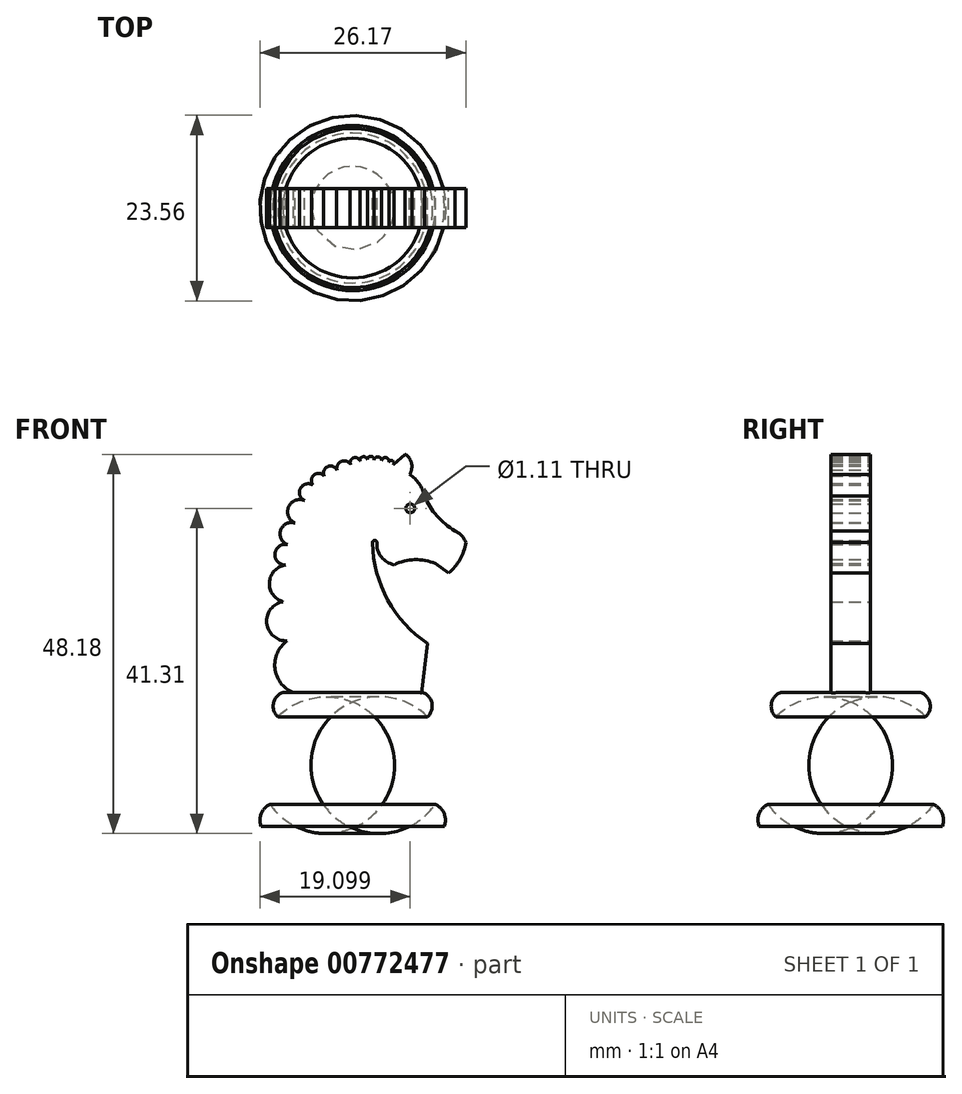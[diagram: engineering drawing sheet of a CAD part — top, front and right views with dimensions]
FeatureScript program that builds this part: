
annotation { "Feature Type Name" : "Feature", "Feature Type Description" : "" }
export const myFeature = defineFeature(function(context is Context, id is Id, definition is map)
    precondition{}
    {
        {
            var Q0;
            Q0=qCreatedBy(makeId("Front.planeOp"),FACE);
            var sketch = newSketch(context, id + "F0", { "sketchPlane" : qUnion([Q0])});
            skArc(sketch, "E0", {"start": v(-7.5, 42.75) * mm, "mid": v(-9.76, 30.83) * mm, "end": v(-7.05, 19.01) * mm});
            skArc(sketch, "E1", {"start": v(-1.21, 48.3) * mm, "mid": v(-4.94, 46.2) * mm, "end": v(-7.5, 42.75) * mm});
            skArc(sketch, "E2", {"start": v(4.28, 48.3) * mm, "mid": v(1.53, 48.79) * mm, "end": v(-1.21, 48.3) * mm});
            skLineSegment(sketch, "E3", {"start": v(7.79, 18.88) * mm, "end": v(8.6, 25.55) * mm});
            skArc(sketch, "E4", {"start": v(1.6, 38.32) * mm, "mid": v(3.5, 31.06) * mm, "end": v(8.6, 25.55) * mm});
            skArc(sketch, "E5", {"start": v(2.13, 38.38) * mm, "mid": v(1.83, 38.62) * mm, "end": v(1.6, 38.32) * mm});
            skArc(sketch, "E6", {"start": v(2.13, 38.38) * mm, "mid": v(2.7, 36.53) * mm, "end": v(4.36, 35.53) * mm});
            skArc(sketch, "E7", {"start": v(6.3, 47) * mm, "mid": v(6.55, 48.4) * mm, "end": v(5.74, 49.56) * mm});
            skLineSegment(sketch, "E8", {"start": v(4.28, 48.3) * mm, "end": v(5.74, 49.56) * mm});
            skArc(sketch, "E9", {"start": v(8.2, 44.27) * mm, "mid": v(7.5, 45.82) * mm, "end": v(6.3, 47) * mm});
            skArc(sketch, "E10", {"start": v(8.2, 44.27) * mm, "mid": v(9.77, 41.74) * mm, "end": v(12.07, 39.84) * mm});
            skArc(sketch, "E11", {"start": v(13.45, 38.34) * mm, "mid": v(12.9, 39.23) * mm, "end": v(12.07, 39.84) * mm});
            skArc(sketch, "E12", {"start": v(11.27, 34.47) * mm, "mid": v(12.7, 36.22) * mm, "end": v(13.45, 38.34) * mm});
            skArc(sketch, "E13", {"start": v(9.58, 35.67) * mm, "mid": v(6.95, 36.18) * mm, "end": v(4.36, 35.53) * mm});
            skLineSegment(sketch, "E14", {"start": v(9.58, 35.67) * mm, "end": v(11.27, 34.47) * mm});
            skLineSegment(sketch, "E15", {"start": v(-7.05, 19.01) * mm, "end": v(7.8, 19.01) * mm});
            skPoint(sketch, "E16.end.orphan", {"position": v(7.79, 16.62) * mm});
            skPoint(sketch, "E17.start.orphan", {"position": v(-7.5, 16.63) * mm});
            skLineSegment(sketch, "E18", {"start": v(8.67, 37.4) * mm, "end": v(11.27, 35.67) * mm});
            skCircle(sketch, "E19", {"center": v(6.38, 42.7) * mm, "radius": 0.56 * mm});
            skPoint(sketch, "E20.start.orphan", {"position": v(-11.68, 44.88) * mm});
            skPoint(sketch, "E21.end.orphan", {"position": v(-11.68, 43.37) * mm});
            skPoint(sketch, "E22.end.orphan", {"position": v(-11.68, 41.65) * mm});
            skPoint(sketch, "E23.start.orphan", {"position": v(-11.68, 39.8) * mm});
            skPoint(sketch, "E24.end.orphan", {"position": v(-8.9, 38.46) * mm});
            skPoint(sketch, "E24.start.orphan", {"position": v(-11.68, 38.46) * mm});
            skPoint(sketch, "E25.end.orphan", {"position": v(-11.68, 37.05) * mm});
            skPoint(sketch, "E26.orphan", {"position": v(-11.68, 35.66) * mm});
            skPoint(sketch, "E27.end.orphan", {"position": v(-9.5, 34.37) * mm});
            skPoint(sketch, "E28.end.orphan", {"position": v(-11.68, 34.37) * mm});
            skPoint(sketch, "E29.end.orphan", {"position": v(-11.68, 32.72) * mm});
            skPoint(sketch, "E30.end.orphan", {"position": v(-11.68, 30.9) * mm});
            skPoint(sketch, "E31.end.orphan", {"position": v(-11.68, 28.54) * mm});
            skPoint(sketch, "E32.end.orphan", {"position": v(-9.5, 27.44) * mm});
            skPoint(sketch, "E33.end.orphan", {"position": v(-11.68, 26.74) * mm});
            skArc(sketch, "E34", {"start": v(-7.01, 43.67) * mm, "mid": v(-9.08, 42.86) * mm, "end": v(-8.22, 40.82) * mm});
            skArc(sketch, "E35", {"start": v(-8.22, 40.82) * mm, "mid": v(-10.11, 39.85) * mm, "end": v(-9, 38.04) * mm});
            skArc(sketch, "E36", {"start": v(-9, 38.04) * mm, "mid": v(-10.78, 37.05) * mm, "end": v(-9.48, 35.49) * mm});
            skArc(sketch, "E37", {"start": v(-9.48, 35.49) * mm, "mid": v(-11.52, 33.27) * mm, "end": v(-9.76, 30.83) * mm});
            skArc(sketch, "E38", {"start": v(-9.76, 30.83) * mm, "mid": v(-11.86, 28.1) * mm, "end": v(-9.25, 25.87) * mm});
            skPoint(sketch, "E39.start.orphan", {"position": v(-8.9, 46.81) * mm});
            skPoint(sketch, "E40.end.orphan", {"position": v(-7.05, 48.12) * mm});
            skPoint(sketch, "E41.start.orphan", {"position": v(-4.94, 46.2) * mm});
            skPoint(sketch, "E42.end.orphan", {"position": v(0, 48.64) * mm});
            skPoint(sketch, "E43.start.orphan", {"position": v(1.53, 48.79) * mm});
            skArc(sketch, "E44", {"start": v(-5.72, 45.42) * mm, "mid": v(-7.48, 45.37) * mm, "end": v(-7.01, 43.67) * mm});
            skArc(sketch, "E45", {"start": v(-4.43, 46.61) * mm, "mid": v(-5.88, 46.9) * mm, "end": v(-5.72, 45.42) * mm});
            skArc(sketch, "E46", {"start": v(-2.94, 47.58) * mm, "mid": v(-4.23, 47.94) * mm, "end": v(-4.43, 46.61) * mm});
            skArc(sketch, "E47", {"start": v(-1.21, 48.3) * mm, "mid": v(-2.37, 48.65) * mm, "end": v(-2.94, 47.58) * mm});
            skArc(sketch, "E48", {"start": v(0, 48.64) * mm, "mid": v(-0.8, 49.13) * mm, "end": v(-1.21, 48.3) * mm});
            skArc(sketch, "E49", {"start": v(0.93, 48.77) * mm, "mid": v(0.4, 49.26) * mm, "end": v(0, 48.64) * mm});
            skArc(sketch, "E50", {"start": v(1.79, 48.79) * mm, "mid": v(1.35, 49.3) * mm, "end": v(0.93, 48.77) * mm});
            skArc(sketch, "E51", {"start": v(2.75, 48.7) * mm, "mid": v(2.32, 49.24) * mm, "end": v(1.79, 48.79) * mm});
            skArc(sketch, "E52", {"start": v(3.65, 48.5) * mm, "mid": v(3.32, 49.14) * mm, "end": v(2.75, 48.7) * mm});
            skArc(sketch, "E53", {"start": v(4.28, 48.3) * mm, "mid": v(4.08, 48.76) * mm, "end": v(3.65, 48.5) * mm});
            skArc(sketch, "E54", {"start": v(-9.25, 25.87) * mm, "mid": v(-9.52, 25.9) * mm, "end": v(-9.8, 25.9) * mm});
            skArc(sketch, "E55", {"start": v(-9.25, 25.87) * mm, "mid": v(-10.65, 21.64) * mm, "end": v(-7.05, 19.01) * mm});
            skSolve(sketch);
        }
        {
            var Q0;
            Q0=qSketchRegion(id+"F0",true);
            extrude(context, id + "F1", {"entities" : qUnion([Q0]), "endBound" : BoundingType.SYMMETRIC, "depth" : 5 * mm, "offsetDistance" : 25 * mm});
        }
        {
            var Q0;
            Q0=qCreatedBy(makeId("Front.planeOp"),FACE);
            var sketch = newSketch(context, id + "F2", { "sketchPlane" : qUnion([Q0])});
            skArc(sketch, "E56", {"start": v(-9.8, 19.32) * mm, "mid": v(-11, 17.95) * mm, "end": v(-10.44, 16.22) * mm});
            skArc(sketch, "E57", {"start": v(-10.44, 16.22) * mm, "mid": v(-12.96, 10.83) * mm, "end": v(-11.42, 5.08) * mm});
            skArc(sketch, "E58", {"start": v(-11.42, 5.08) * mm, "mid": v(-12.55, 3.92) * mm, "end": v(-12.57, 2.3) * mm});
            skLineSegment(sketch, "E59", {"start": v(-12.57, 2.3) * mm, "end": v(-0.93, 2.3) * mm});
            skLineSegment(sketch, "E60", {"start": v(-0.93, 2.3) * mm, "end": v(-0.93, 3.78) * mm});
            skLineSegment(sketch, "E61", {"start": v(-0.93, 19.3) * mm, "end": v(-0.93, 2.3) * mm});
            skLineSegment(sketch, "E62", {"start": v(-0.93, 19.3) * mm, "end": v(-9.8, 19.32) * mm});
            skSolve(sketch);
        }
        {
            var Q0;
            Q0=qSketchRegion(id+"F2",true);
            var Q1;
            Q1=sQuery(id+"F2.wireOp",EDGE,"E61");
            revolve(context, id + "F3", {"operationType" : NewBodyOperationType.ADD, "surfaceOperationType" : NewSurfaceOperationType.NEW, "entities" : qUnion([Q0]), "axis" : qUnion([Q1]), "revolveType" : RevolveType.FULL});
        }
    });
